# Revit family: ProxWay_Считыватель_карт_Mifare_с_поддержкой_BLE_PW-102 MF_G
name_source: partatom
category: Охранная сигнализация
units: mm (PartAtom-declared; Revit-internal decimal feet)

## family parameters
Всегда вертикально = Нет
На основе рабочей плоскости = Нет
Общий = Да
При загрузке вырезать с полостями = Нет
Размер круглого соединителя = Использовать диаметр
Сохранять ориентацию аннотаций = Нет
Тип детали = Нормальный
Точка расчета площади = Да

## types (1)
- PW-102 MF G_серый
    =Габариты= = =Габариты=
    ADSK_Единица измерения = шт.
    ADSK_Завод-изготовитель = ProxWay
    ADSK_Код изделия = Серый
    ADSK_Количество = 1
    ADSK_Марка = PW-102 MF G
    ADSK_Материал = Серый
    ADSK_Наименование = Считыватель карт Mifare
    ADSK_Напряжение = 12 В
    ADSK_Обозначение = RD
    ADSK_Раздел спецификации = 3. Периферийное оборудование
    ADSK_Размер_Высота = 120 мм
    ADSK_Размер_Глубина = 20 мм
    ADSK_Размер_Ширина = 48 мм
    ADSK_Тип = PW-102 MF G
    ADSK_Ток дежурного режима = 50.000 мА
    ADSK_Ток тревожного режима = 50.000 мА
    URL = https://proxway-ble.ru
    Зона обслуживания_Отступ от прибора = 50 мм
    Отметка по умолчанию = 0 мм
    Текст = PW-102 MF
    УГО_Тип = УГО_Считыватель
